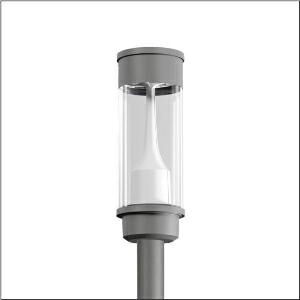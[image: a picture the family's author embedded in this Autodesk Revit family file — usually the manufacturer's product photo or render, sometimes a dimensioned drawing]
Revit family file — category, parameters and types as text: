
# Revit family: litepole_iq___p1_0a_5xa5415nf14h_8c95
name_source: partatom
category: Lighting Fixtures
units: mm (PartAtom-declared; Revit-internal decimal feet)

## family parameters
Cut with Voids When Loaded = No
Host = Face
Light Source = No
Part Type = Normal
Room Calculation Point = No
Round Connector Dimension = Use Diameter
Shared = No

## types (1)
- --- (1 x LED, 1510 lm, 11.8 W, 2700K)
    Apparent Load = 12 VA
    CIE Flux Codes = 32 61 90 93 100
    Color Rendering = 70
    Color Temperature = 2700K
    Default Elevation = 1800 mm
    Description = Litepole iQ, mast luminaire, Module 540 iQ-SR, primary light control with 3 zone facetted reflector, of plastic, silver coated, highly specular, structured, primary optical cover: cover, of PMMA, transparent, partly coated, light distribution: P1.0a, light emission: direct distribution, primary light characteristic: strongly asymmetric, installation type: post-top, LED, High Power LED, rated luminous flux: 1.510lm, luminous efficacy: 128lm/W, light colour: 727, colour temperature: 2700K, control gear: ECG iQ, control: optimised constant luminous flux control (CLO 2.0), Desk-Remote (wireless, voltage-free reading and setting of iQ features in the workshop via application-optimized NFC function/RFID function), Light-Fading, Smart-Wire, Night-Set, Lumen-Switch, Temp-Guard, Auto-Match, Street-Remote, presetting dimming logarithmic, with terminal, 6-pole, max. 2.5mm², mains connection: 230..240V, AC, 50/60Hz, start of lifetime: 12W, end of service life: 12W, reduction: 6W, luminaire housing, upper part, of glass-fibre reinforced polyester, coated, Siteco® metallic grey (DB 702S), diameter: 210mm, height: 590mm, spigot size: d x l = 76 x 70mm (post-top) | with reducer (optional accessory) 60 x 70mm, post-top mast mounting element, of diecast aluminium, coated, Siteco® metallic grey (DB 702S), Module 540 iQ-SR, traffic white (RAL 9016), equipment: standard, protection rating (complete): IP65, insulation class (complete): insulation class II (safety insulation), certification: CE, ENEC, VDE, packaging unit: 1 piece

Light Distribution: P1.0a
    Height = 590 mm
    Lamp = 1 x LED
    Lamp Light Flux = 1510 lm
    Lamp Power = 11.8 W
    Lamp count = 1
    Length = 220 mm
    Luminous efficacy = 128 lm/W
    Manufacturer = Siteco
    ModVariant = No
    Model = 5XA5415NF14H
    Number of Poles = 1
    OnlyDefault = Yes
    Power Factor = 1
    Product Name = Litepole iQ | P1.0a
    Product group = mast luminaire | pylon top
    ProductGroupID = 6100
    Protection Class = Protection class II
    Protection Degree = IP 65
    RLX_Detail_Level = 1
    RLX_Emergency_Light_Flux = 0 lm
    RLX_Emergency_Type = 0
    RLX_Emergency_Type_DB = No
    RlxData = <blob elided: 63913 chars, md5=ffdb95b6>
    Socket = socket
    Standby Power = 0 W
    System Light Flux = 1510 lm
    System Power = 12 W
    Type Comments = factory setting: luminous flux: 100 % | dim-lin: 254 | 472 mA
    Type Image = l_1006025.jpg
    URL = http://relux.com
    VarID = @adj_103147
    Voltage = 0 V
    Weight = 0.00 kg
    Width = 0 mm  [stored 0 ft]

note: [stored X ft] marks values corroborated as IEEE doubles in the binary element streams (Revit-internal decimal feet)

## geometry (parser evidence)
native form markers: Blend x4, Sweep x14
no freeform markers — native parametric forms only
